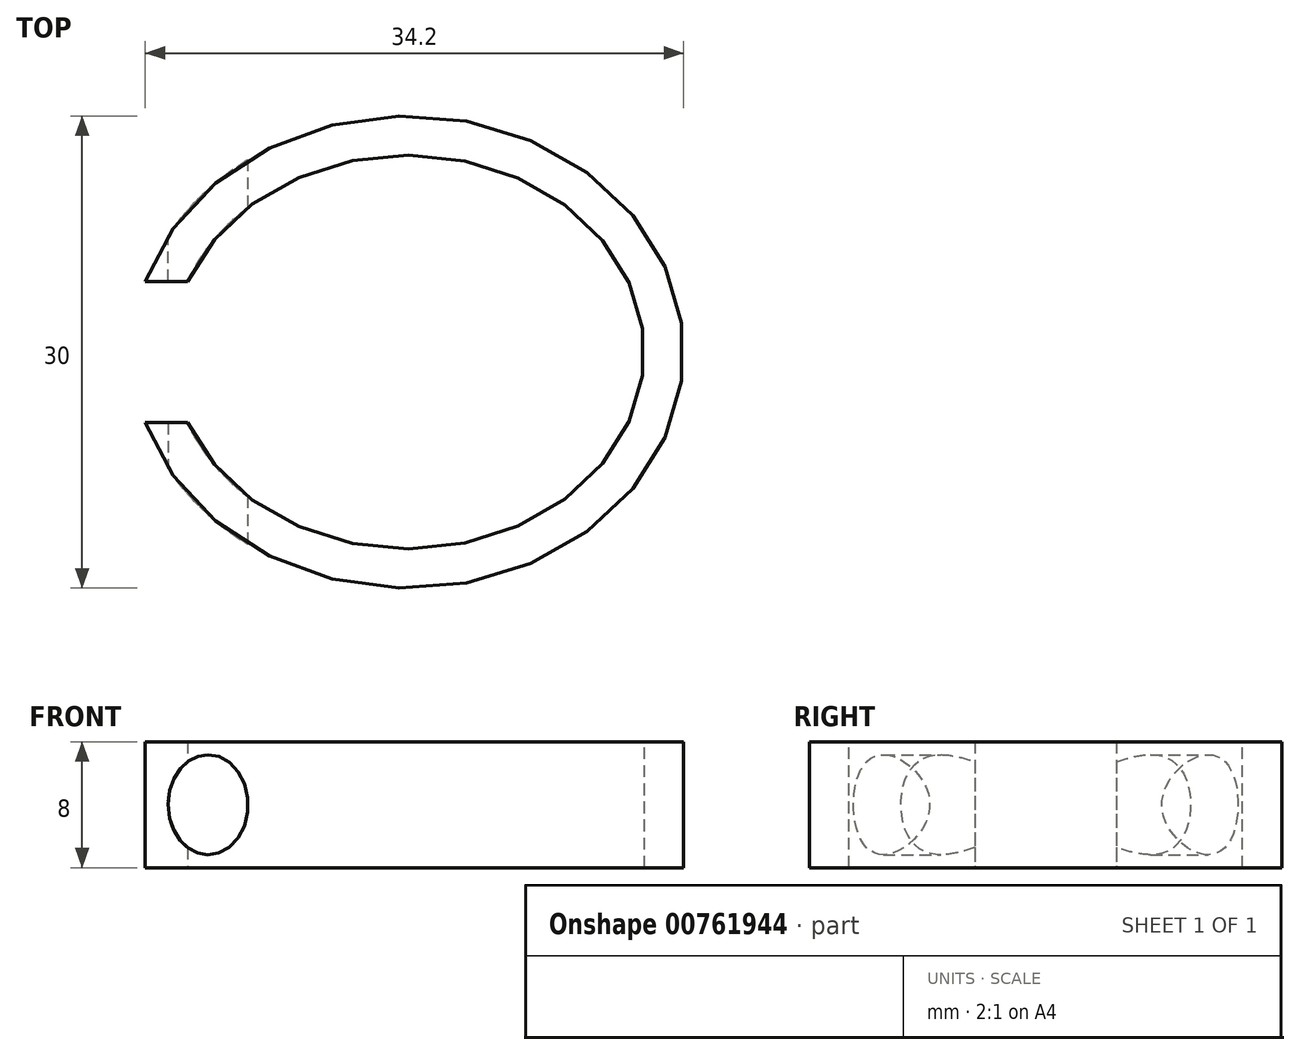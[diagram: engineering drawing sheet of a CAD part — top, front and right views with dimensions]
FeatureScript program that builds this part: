
annotation { "Feature Type Name" : "Feature", "Feature Type Description" : "" }
export const myFeature = defineFeature(function(context is Context, id is Id, definition is map)
    precondition{}
    {
        {
            var Q0;
            Q0=qCreatedBy(makeId("Top.planeOp"),FACE);
            var sketch = newSketch(context, id + "F0", { "sketchPlane" : qUnion([Q0])});
            skEllipse(sketch, "E0", {"center": v(0, 0) * mm, "majorRadius": 17.5 * mm, "minorRadius": 15 * mm, "majorAxis": v(-1, 0)});
            skEllipse(sketch, "E1", {"center": v(0, 0) * mm, "majorRadius": 15 * mm, "minorRadius": 12.5 * mm, "majorAxis": v(-1, 0)});
            skSolve(sketch);
        }
        {
            var Q0;
            Q0=qCreatedBy(makeId("Right.planeOp"),FACE);
            var sketch = newSketch(context, id + "F1", { "sketchPlane" : qUnion([Q0])});
            skLineSegment(sketch, "E2.bottom", {"start": v(-13.5, 2) * mm, "end": v(-10, 2) * mm});
            skLineSegment(sketch, "E2.top", {"start": v(-13.5, -2) * mm, "end": v(-10, -2) * mm});
            skLineSegment(sketch, "E2.left", {"start": v(-13.5, 2) * mm, "end": v(-13.5, -2) * mm});
            skLineSegment(sketch, "E2.right", {"start": v(-10, 2) * mm, "end": v(-10, -2) * mm});
            skPoint(sketch, "E2.middle", {"position": v(-11.75, 0) * mm});
            skSolve(sketch);
        }
        {
            var Q0;
            Q0=makeQuery(id+"F0.imprint","IMPRINT",FACE,{"disambiguationData":[TD([[makeQuery(id+"F0.imprint","IMPRINT",EDGE,{"derivedFrom":sQuery(id+"F0.wireOp",EDGE,"E0")}),1.0]])]});
            extrude(context, id + "F2", {"entities" : qUnion([Q0]), "endBound" : BoundingType.SYMMETRIC, "depth" : 8 * mm, "offsetDistance" : 25.4 * mm});
        }
        {
            var Q0;
            Q0=qCreatedBy(makeId("Top.planeOp"),FACE);
            var sketch = newSketch(context, id + "F3", { "sketchPlane" : qUnion([Q0])});
            skLineSegment(sketch, "E3.bottom", {"start": v(-21.02, 4.49) * mm, "end": v(-9.76, 4.49) * mm});
            skLineSegment(sketch, "E3.top", {"start": v(-21.02, -4.49) * mm, "end": v(-9.76, -4.49) * mm});
            skLineSegment(sketch, "E3.left", {"start": v(-21.02, 4.49) * mm, "end": v(-21.02, -4.49) * mm});
            skLineSegment(sketch, "E3.right", {"start": v(-9.76, 4.49) * mm, "end": v(-9.76, -4.49) * mm});
            skPoint(sketch, "E3.middle", {"position": v(-15.4, 0) * mm});
            skPoint(sketch, "E4.middle", {"position": v(-25.36, 0) * mm});
            skSolve(sketch);
        }
        {
            var Q0;
            Q0 = qSketchRegion(id + "F3", true);
            extrude(context, id + "F4", {"entities" : qUnion([Q0]), "operationType" : NewBodyOperationType.REMOVE, "endBound" : BoundingType.SYMMETRIC, "oppositeDirection" : true, "depth" : 25.4 * mm, "offsetDistance" : 25.4 * mm});
        }
        {
            var Q0;
            Q0=qCreatedBy(makeId("Front.planeOp"),FACE);
            var sketch = newSketch(context, id + "F5", { "sketchPlane" : qUnion([Q0])});
            skEllipse(sketch, "E5", {"center": v(-12.7, 0) * mm, "majorRadius": 3.18 * mm, "minorRadius": 2.54 * mm, "majorAxis": v(0, 1)});
            skSolve(sketch);
        }
        {
            var Q0;
            Q0 = qSketchRegion(id + "F5", true);
            extrude(context, id + "F6", {"entities" : qUnion([Q0]), "operationType" : NewBodyOperationType.REMOVE, "endBound" : BoundingType.SYMMETRIC, "depth" : 25.4 * mm, "offsetDistance" : 25.4 * mm});
        }
    });
